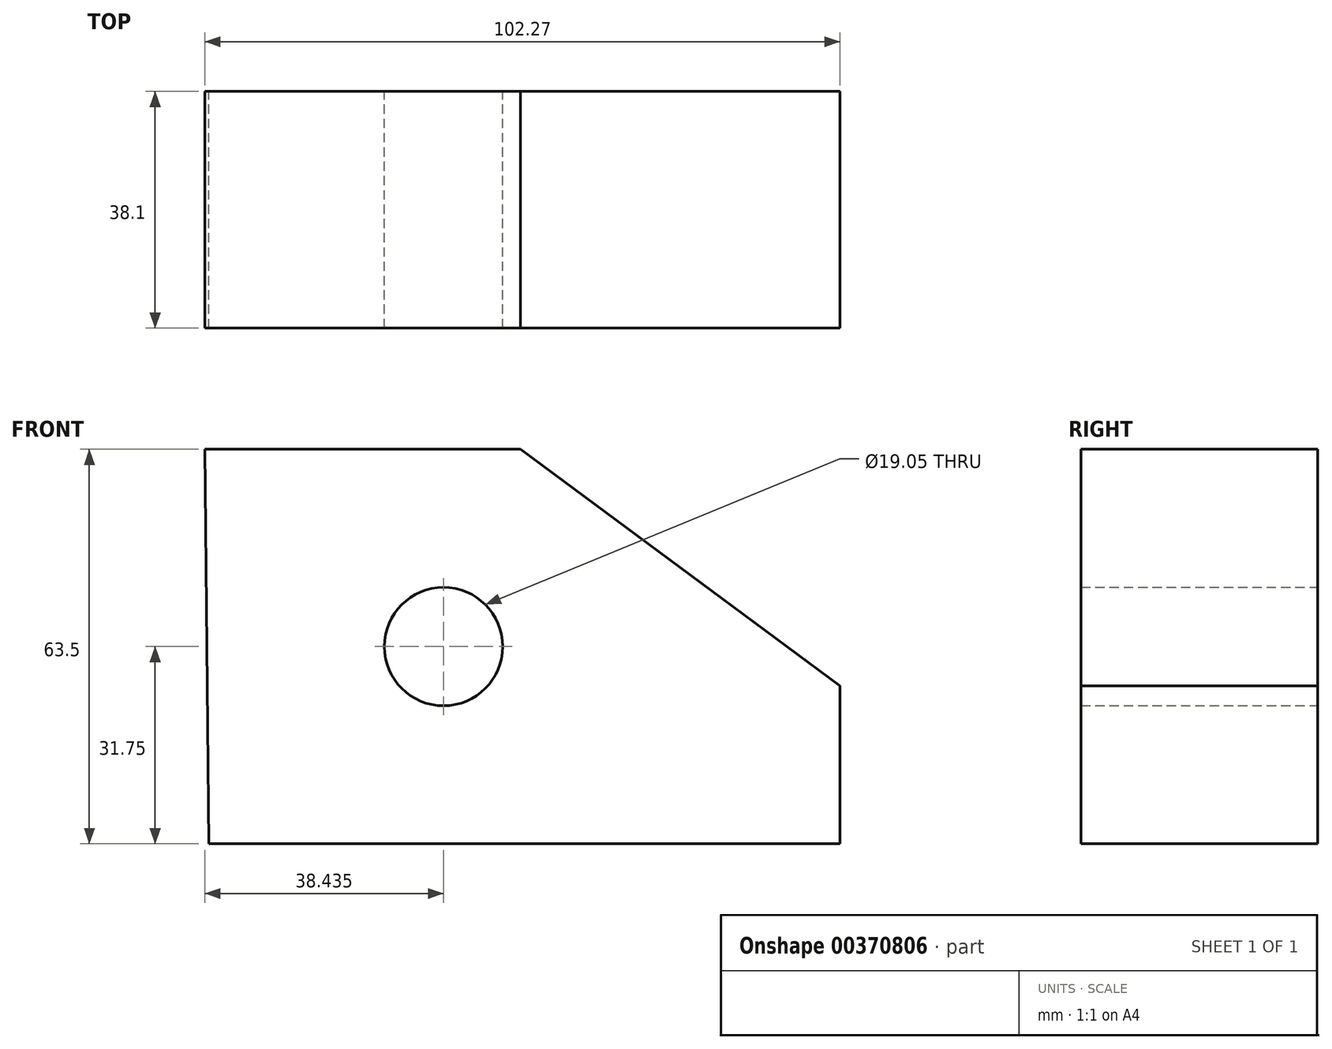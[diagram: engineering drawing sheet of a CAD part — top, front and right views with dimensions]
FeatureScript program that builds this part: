
annotation { "Feature Type Name" : "Feature", "Feature Type Description" : "" }
export const myFeature = defineFeature(function(context is Context, id is Id, definition is map)
    precondition{}
    {
        {
            var Q0;
            Q0=qCreatedBy(makeId("Front.planeOp"),FACE);
            var sketch = newSketch(context, id + "F0", { "sketchPlane" : qUnion([Q0])});
            skLineSegment(sketch, "E0", {"start": v(-50.8, 63.5) * mm, "end": v(0, 63.5) * mm});
            skLineSegment(sketch, "E1", {"start": v(0, 63.5) * mm, "end": v(51.47, 25.4) * mm});
            skLineSegment(sketch, "E2", {"start": v(51.47, 25.4) * mm, "end": v(51.47, 0) * mm});
            skLineSegment(sketch, "E3", {"start": v(51.47, 0) * mm, "end": v(-50.13, 0) * mm});
            skLineSegment(sketch, "E4", {"start": v(-50.13, 0) * mm, "end": v(-50.8, 63.5) * mm});
            skCircle(sketch, "E5", {"center": v(-12.36, 31.75) * mm, "radius": 9.53 * mm});
            skSolve(sketch);
        }
        {
            var Q0;
            Q0=makeQuery(id+"F0.imprint","IMPRINT",FACE,{"disambiguationData":[TD([[makeQuery(id+"F0.imprint","IMPRINT",EDGE,{"derivedFrom":sQuery(id+"F0.wireOp",EDGE,"E0")}),-1.0]])]});
            extrude(context, id + "F1", {"entities" : qUnion([Q0]), "depth" : 38.1 * mm});
        }
    });
